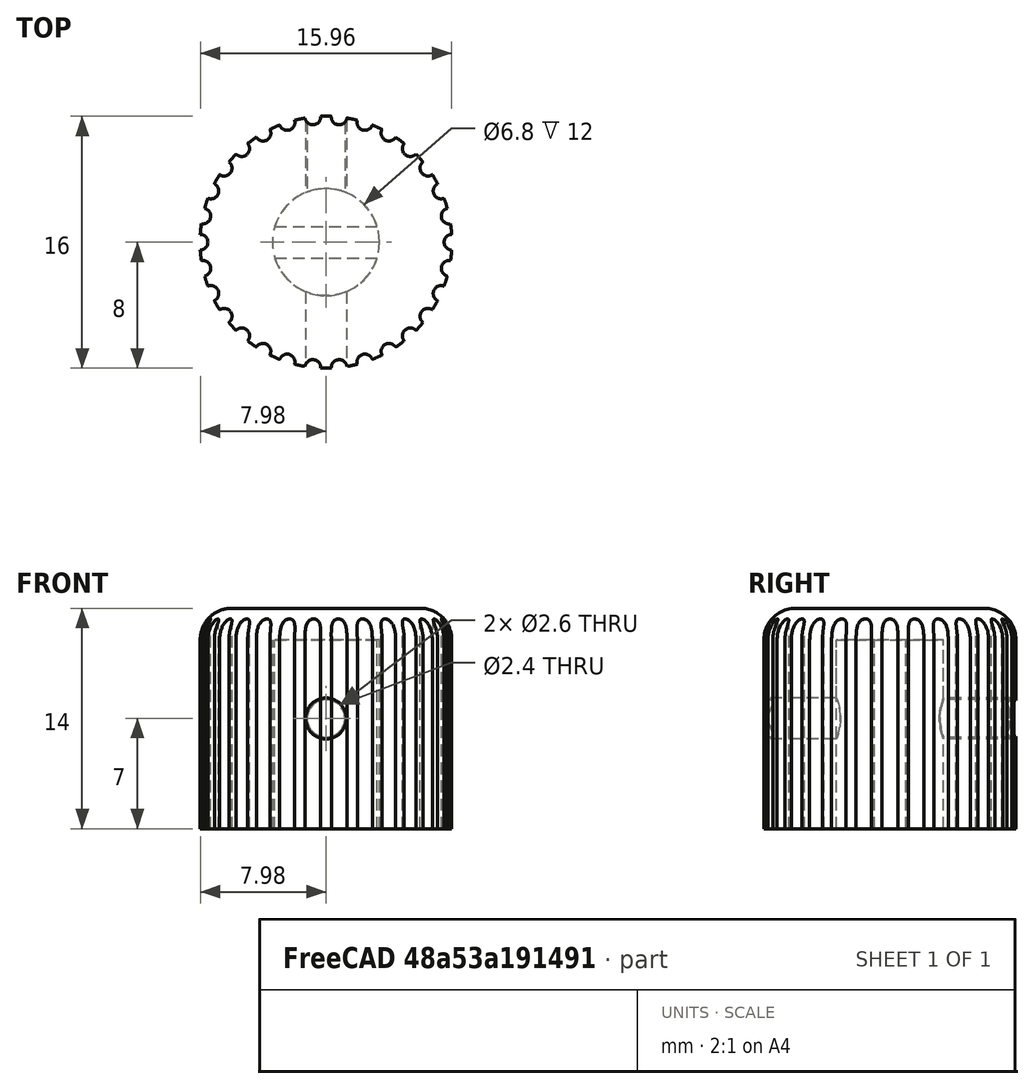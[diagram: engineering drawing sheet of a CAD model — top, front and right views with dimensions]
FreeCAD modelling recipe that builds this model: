
FCSTD DOCUMENT  (FreeCAD 0.17R13522 (Git))
Label: v5_perilla2_chica
License: CreativeCommons Attribution-ShareAlike
LicenseURL: http://creativecommons.org/licenses/by-sa/4.0/
objects: Part::Cut×8, Part::Cylinder×4, Part::Feature×2, Part::Fillet×1, Part::FeaturePython×1, Part::Box×1, Part::Fuse×1
note: 18 computed .brp shape members not serialized (recipe doc carries the construction recipe); baked Part::Feature solids carry a one-line shape summary decoded from their .brp

FEATURE [Part::Cylinder] Cylinder
  Angle = 360
  AttacherType = Attacher::AttachEngine3D
  Height = 14
  Radius = 8
FEATURE [Part::Cylinder] Cylinder001  label="perfora centro"
  Angle = 360
  AttacherType = Attacher::AttachEngine3D
  Height = 13
  Placement = pos=(0,0,-1) rot=(0,0,1;0rad)
  Radius = 3.4
FEATURE [Part::Cut] Cut
  Base = -> Cylinder
  Refine = true
  Tool = -> Cylinder001
FEATURE [Part::Cylinder] Cylinder002  label="barilla borde"
  Angle = 360
  AttacherType = Attacher::AttachEngine3D
  Height = 20
  Placement = pos=(-8,0,-1) rot=(0,0,1;0rad)
  Radius = 0.5
FEATURE [Part::Fillet] Fillet
  Base = -> Cut
  Edges = 1 edges r=2: [Edge1]
FEATURE [Part::FeaturePython] Array  # Draft array (typed FeaturePython)
  Angle = 360
  ArrayType = 1
  Axis = (0,0,1)
  Base = -> Cylinder002
  Center = (0,0,0)
  Fuse = false
  IntervalAxis = (0,0,0)
  IntervalX = (1,0,0)
  IntervalY = (0,1,0)
  IntervalZ = (0,0,0)
  NumberPolar = 30
  NumberX = 2
  NumberY = 2
  NumberZ = 1
FEATURE [Part::Cut] Cut001  label="boton sin agujeros allen"
  Base = -> Fillet
  Refine = true
  Tool = -> Array
FEATURE [Part::Feature] Cylinder001005001  label="barilla perfora alen001"
  Placement = pos=(0,27,7) rot=(1,0,0;1.5708rad)
  shape: bbox 2.4 x 26 x 2.4 mm, 3 faces (baked)
FEATURE [Part::Cut] Cut002  label="old base con un agujero para allen"
  Base = -> Cut001
  Refine = true
  Tool = -> Cylinder001005001
FEATURE [Part::Cut] Cut003
  Base = -> Fillet
  Refine = true
  Tool = -> Array
FEATURE [Part::Cut] Cut004  label="perilla con un agujero allen"
  Base = -> Cut003
  Refine = true
  Tool = -> Cylinder001005001
FEATURE [Part::Cylinder] Cylinder001005002  label="barilla perforadora 2.6mm diametro"
  Angle = 360
  AttacherType = Attacher::AttachEngine3D
  Height = 20
  Placement = pos=(0,-2,7) rot=(1,0,0;1.5708rad)
  Radius = 1.3
FEATURE [Part::Cut] Cut005  label="perilla chica"
  Base = -> Cut004
  Refine = true
  Tool = -> Cylinder001005002
FEATURE [Part::Box] Box  label="Cube"
  AttacherType = Attacher::AttachEngine3D
  Height = 12
  Length = 10
  Placement = pos=(-5,-1,0) rot=(0,0,1;0rad)
  Width = 2
FEATURE [Part::Fuse] Fusion  label="perilla con aletas"
  Base = -> Cut005
  Refine = true
  Tool = -> Box
FEATURE [Part::Feature] Cylinder001005002001  label="barilla perforadora 2.6mm diametro001"
  Placement = pos=(0,22,7) rot=(1,0,0;1.5708rad)
  shape: bbox 2.6 x 20 x 2.6 mm, 3 faces (baked)
FEATURE [Part::Cut] Cut006
  Base = -> Fusion
  Refine = true
  Tool = -> Cylinder001005002001
FEATURE [Part::Cut] Cut007  label="perilla chica con 2 agujeros allen y aletas"
  Base = -> Cut006
  Refine = true
  Tool = -> Cylinder001005002
